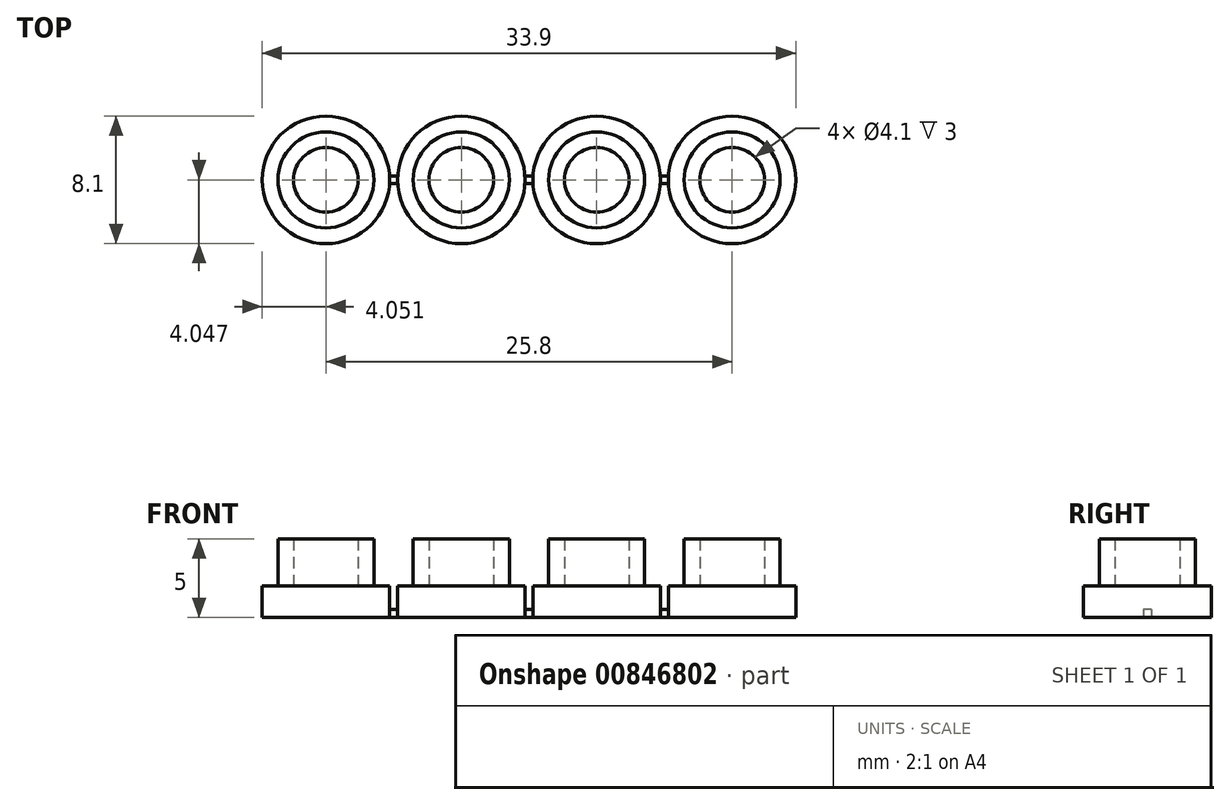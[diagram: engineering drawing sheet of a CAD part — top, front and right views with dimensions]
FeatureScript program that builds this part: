
annotation { "Feature Type Name" : "Feature", "Feature Type Description" : "" }
export const myFeature = defineFeature(function(context is Context, id is Id, definition is map)
    precondition{}
    {
        {
            var Q0;
            Q0=qCreatedBy(makeId("Top.planeOp"),FACE);
            var sketch = newSketch(context, id + "F0", { "sketchPlane" : qUnion([Q0])});
            skCircle(sketch, "E0", {"center": v(-31.29, -23.1) * mm, "radius": 2.05 * mm});
            skCircle(sketch, "E1", {"center": v(-31.29, -23.1) * mm, "radius": 3.05 * mm});
            skCircle(sketch, "E2", {"center": v(-31.29, -23.1) * mm, "radius": 4.05 * mm});
            skCircle(sketch, "E3.1.0.0", {"center": v(-22.69, -23.1) * mm, "radius": 4.05 * mm});
            skCircle(sketch, "E3.1.0.1", {"center": v(-22.69, -23.1) * mm, "radius": 3.05 * mm});
            skCircle(sketch, "E3.1.0.2", {"center": v(-22.69, -23.1) * mm, "radius": 2.05 * mm});
            skCircle(sketch, "E3.2.0.0", {"center": v(-14.09, -23.1) * mm, "radius": 4.05 * mm});
            skCircle(sketch, "E3.2.0.1", {"center": v(-14.09, -23.1) * mm, "radius": 3.05 * mm});
            skCircle(sketch, "E3.2.0.2", {"center": v(-14.09, -23.1) * mm, "radius": 2.05 * mm});
            skCircle(sketch, "E3.3.0.0", {"center": v(-5.49, -23.1) * mm, "radius": 4.05 * mm});
            skCircle(sketch, "E3.3.0.1", {"center": v(-5.49, -23.1) * mm, "radius": 3.05 * mm});
            skCircle(sketch, "E3.3.0.2", {"center": v(-5.49, -23.1) * mm, "radius": 2.05 * mm});
            skLineSegment(sketch, "E3.direction1", {"start": v(-31.29, -23.1) * mm, "end": v(-22.69, -23.1) * mm, "construction": true});
            skPoint(sketch, "E4", {"position": v(-27.24, -23.1) * mm});
            skPoint(sketch, "E5", {"position": v(-26.74, -23.1) * mm});
            skPoint(sketch, "E6", {"position": v(-26.99, -23.1) * mm});
            skLineSegment(sketch, "E7.bottom", {"start": v(-26.73, -22.84) * mm, "end": v(-27.25, -22.84) * mm});
            skLineSegment(sketch, "E7.top", {"start": v(-26.73, -23.34) * mm, "end": v(-27.25, -23.34) * mm});
            skLineSegment(sketch, "E8.1.0.0", {"start": v(-18.13, -23.34) * mm, "end": v(-18.65, -23.34) * mm});
            skLineSegment(sketch, "E8.1.0.1", {"start": v(-18.13, -22.84) * mm, "end": v(-18.65, -22.84) * mm});
            skLineSegment(sketch, "E8.2.0.0", {"start": v(-9.53, -23.34) * mm, "end": v(-10.05, -23.34) * mm});
            skLineSegment(sketch, "E8.2.0.1", {"start": v(-9.53, -22.84) * mm, "end": v(-10.05, -22.84) * mm});
            skLineSegment(sketch, "E8.direction1", {"start": v(-27.25, -23.34) * mm, "end": v(-18.65, -23.34) * mm, "construction": true});
            skSolve(sketch);
        }
        {
            var Q0;
            Q0=makeQuery(id+"F0.imprint","IMPRINT",FACE,{"disambiguationData":[TD([[makeQuery(id+"F0.imprint","IMPRINT",EDGE,{"derivedFrom":sQuery(id+"F0.wireOp",EDGE,"E0")}),-1.0]])]});
            var Q1;
            Q1=makeQuery(id+"F0.imprint","IMPRINT",FACE,{"disambiguationData":[TD([[makeQuery(id+"F0.imprint","IMPRINT",EDGE,{"derivedFrom":sQuery(id+"F0.wireOp",EDGE,"E3.1.0.1")}),1.0]])]});
            var Q2;
            Q2=makeQuery(id+"F0.imprint","IMPRINT",FACE,{"disambiguationData":[TD([[makeQuery(id+"F0.imprint","IMPRINT",EDGE,{"derivedFrom":sQuery(id+"F0.wireOp",EDGE,"E3.2.0.1")}),1.0]])]});
            var Q3;
            Q3=makeQuery(id+"F0.imprint","IMPRINT",FACE,{"disambiguationData":[TD([[makeQuery(id+"F0.imprint","IMPRINT",EDGE,{"derivedFrom":sQuery(id+"F0.wireOp",EDGE,"E3.3.0.1")}),1.0]])]});
            extrude(context, id + "F1", {"entities" : qUnion([Q0, Q1, Q2, Q3]), "depth" : 5 * mm, "offsetDistance" : 25 * mm});
        }
        {
            var Q0;
            Q0=makeQuery(id+"F0.imprint","IMPRINT",FACE,{"disambiguationData":[TD([[makeQuery(id+"F0.imprint","IMPRINT",EDGE,{"derivedFrom":sQuery(id+"F0.wireOp",EDGE,"E0")}),1.0]])]});
            var Q1;
            Q1=makeQuery(id+"F0.imprint","IMPRINT",FACE,{"disambiguationData":[TD([[makeQuery(id+"F0.imprint","IMPRINT",EDGE,{"derivedFrom":sQuery(id+"F0.wireOp",EDGE,"E1")}),-1.0]])]});
            var Q2;
            Q2=makeQuery(id+"F0.imprint","IMPRINT",FACE,{"disambiguationData":[TD([[makeQuery(id+"F0.imprint","IMPRINT",EDGE,{"derivedFrom":sQuery(id+"F0.wireOp",EDGE,"E3.1.0.0")}),1.0]])]});
            var Q3;
            Q3=makeQuery(id+"F0.imprint","IMPRINT",FACE,{"disambiguationData":[TD([[makeQuery(id+"F0.imprint","IMPRINT",EDGE,{"derivedFrom":sQuery(id+"F0.wireOp",EDGE,"E3.1.0.2")}),1.0]])]});
            var Q4;
            Q4=makeQuery(id+"F0.imprint","IMPRINT",FACE,{"disambiguationData":[TD([[makeQuery(id+"F0.imprint","IMPRINT",EDGE,{"derivedFrom":sQuery(id+"F0.wireOp",EDGE,"E3.2.0.0")}),1.0]])]});
            var Q5;
            Q5=makeQuery(id+"F0.imprint","IMPRINT",FACE,{"disambiguationData":[TD([[makeQuery(id+"F0.imprint","IMPRINT",EDGE,{"derivedFrom":sQuery(id+"F0.wireOp",EDGE,"E3.2.0.2")}),1.0]])]});
            var Q6;
            Q6=makeQuery(id+"F0.imprint","IMPRINT",FACE,{"disambiguationData":[TD([[makeQuery(id+"F0.imprint","IMPRINT",EDGE,{"derivedFrom":sQuery(id+"F0.wireOp",EDGE,"E3.3.0.0")}),1.0]])]});
            var Q7;
            Q7=makeQuery(id+"F0.imprint","IMPRINT",FACE,{"disambiguationData":[TD([[makeQuery(id+"F0.imprint","IMPRINT",EDGE,{"derivedFrom":sQuery(id+"F0.wireOp",EDGE,"E3.3.0.2")}),1.0]])]});
            extrude(context, id + "F2", {"entities" : qUnion([Q0, Q1, Q2, Q3, Q4, Q5, Q6, Q7]), "operationType" : NewBodyOperationType.ADD, "depth" : 2 * mm, "offsetDistance" : 25 * mm});
        }
        {
            var Q0;
            {var subQ0=sQuery(id+"F0.wireOp",EDGE,"E7.bottom");Q0=makeQuery(id+"F0.imprint","IMPRINT",FACE,{"disambiguationData":[TD([[makeQuery(id+"F0.imprint","IMPRINT",EDGE,{"derivedFrom":subQ0}),1.0]])]});}
            var Q1;
            {var subQ0=sQuery(id+"F0.wireOp",EDGE,"E8.1.0.0");Q1=makeQuery(id+"F0.imprint","IMPRINT",FACE,{"disambiguationData":[TD([[makeQuery(id+"F0.imprint","IMPRINT",EDGE,{"derivedFrom":subQ0}),-1.0]])]});}
            var Q2;
            {var subQ0=sQuery(id+"F0.wireOp",EDGE,"E8.2.0.0");Q2=makeQuery(id+"F0.imprint","IMPRINT",FACE,{"disambiguationData":[TD([[makeQuery(id+"F0.imprint","IMPRINT",EDGE,{"derivedFrom":subQ0}),-1.0]])]});}
            extrude(context, id + "F3", {"entities" : qUnion([Q0, Q1, Q2]), "depth" : 0.5 * mm, "offsetDistance" : 25 * mm});
        }
    });
